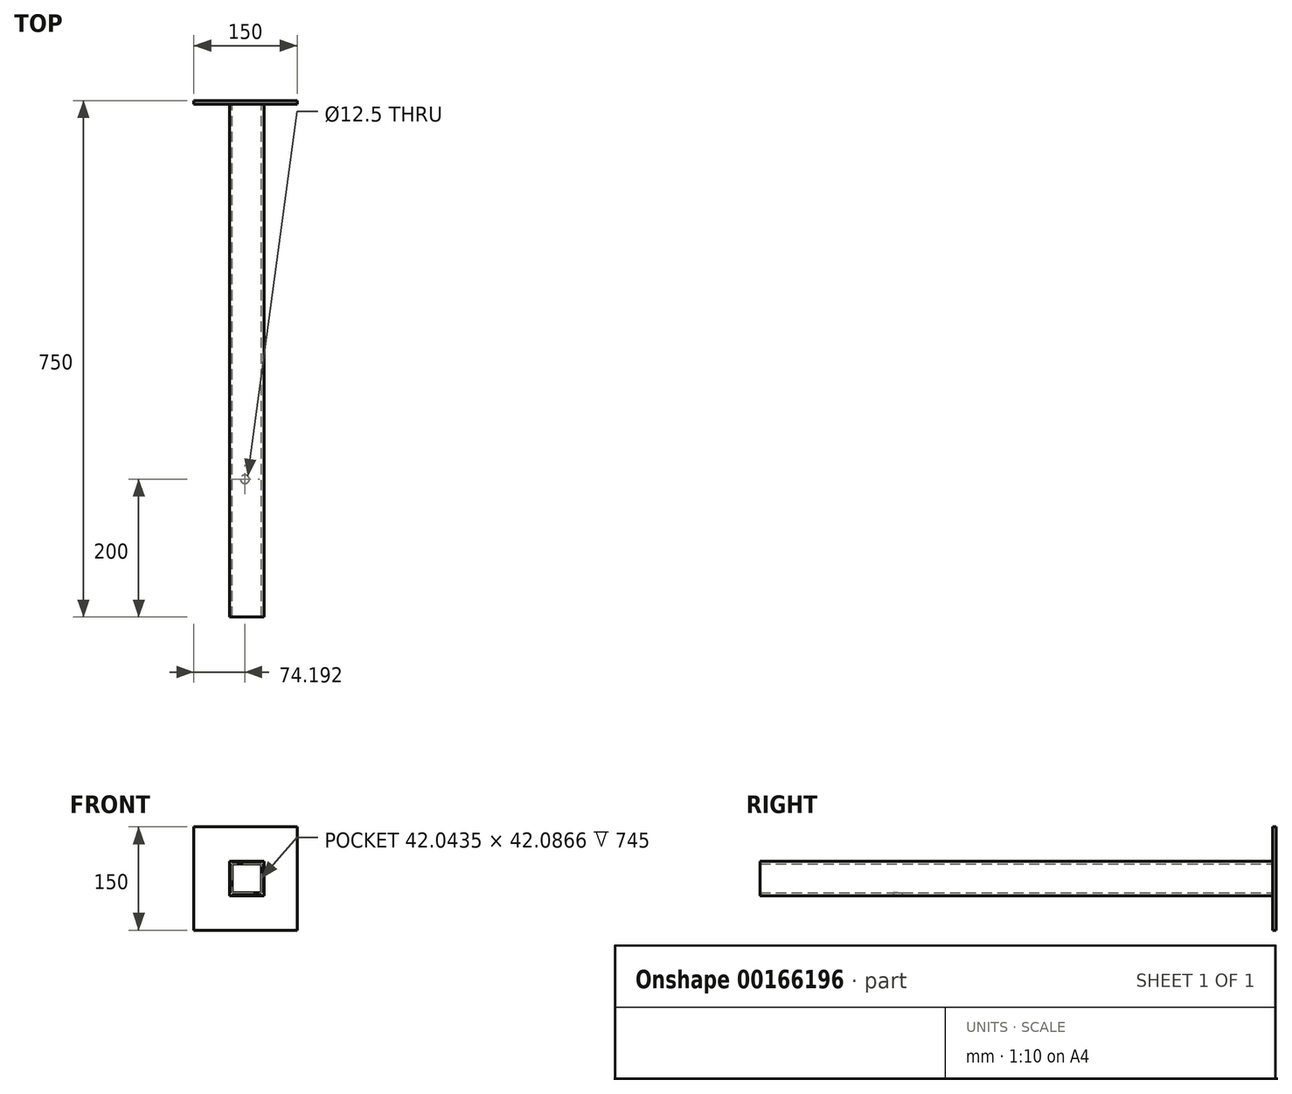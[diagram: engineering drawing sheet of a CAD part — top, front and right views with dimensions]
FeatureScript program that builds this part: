
annotation { "Feature Type Name" : "Feature", "Feature Type Description" : "" }
export const myFeature = defineFeature(function(context is Context, id is Id, definition is map)
    precondition{}
    {
        {
            var Q0;
            Q0=qCreatedBy(makeId("Front.planeOp"),FACE);
            var sketch = newSketch(context, id + "F0", { "sketchPlane" : qUnion([Q0])});
            skLineSegment(sketch, "E0.bottom", {"start": v(-73.02, 50) * mm, "end": v(-23.02, 50) * mm});
            skLineSegment(sketch, "E0.top", {"start": v(-73.02, 0) * mm, "end": v(-23.02, 0) * mm});
            skLineSegment(sketch, "E0.left", {"start": v(-73.02, 50) * mm, "end": v(-73.02, 0) * mm});
            skLineSegment(sketch, "E0.right", {"start": v(-23.02, 50) * mm, "end": v(-23.02, 0) * mm});
            skPoint(sketch, "E1.centerSnap0", {"position": v(-48.02, 50) * mm});
            skLineSegment(sketch, "E2.bottom", {"start": v(-69.17, 46.31) * mm, "end": v(-27.13, 46.31) * mm});
            skLineSegment(sketch, "E2.top", {"start": v(-69.17, 4.23) * mm, "end": v(-27.13, 4.23) * mm});
            skLineSegment(sketch, "E2.left", {"start": v(-69.17, 46.31) * mm, "end": v(-69.17, 4.23) * mm});
            skLineSegment(sketch, "E2.right", {"start": v(-27.13, 46.31) * mm, "end": v(-27.13, 4.23) * mm});
            skSolve(sketch);
        }
        {
            var Q0;
            Q0 = qSketchRegion(id + "F0", true);
            extrude(context, id + "F1", {"entities" : qUnion([Q0]), "depth" : 750 * mm});
        }
        {
            var Q0;
            Q0=qCreatedBy(makeId("Front.planeOp"),FACE);
            var sketch = newSketch(context, id + "F2", { "sketchPlane" : qUnion([Q0])});
            skLineSegment(sketch, "E3.bottom", {"start": v(24.88, -50.14) * mm, "end": v(-125.12, -50.14) * mm});
            skLineSegment(sketch, "E3.top", {"start": v(24.88, 99.86) * mm, "end": v(-125.12, 99.86) * mm});
            skLineSegment(sketch, "E3.left", {"start": v(24.88, -50.14) * mm, "end": v(24.88, 99.86) * mm});
            skLineSegment(sketch, "E3.right", {"start": v(-125.12, -50.14) * mm, "end": v(-125.12, 99.86) * mm});
            skSolve(sketch);
        }
        {
            var Q0;
            Q0=makeQuery(id+"F2.imprint","IMPRINT",FACE,{"disambiguationData":[TD([[makeQuery(id+"F2.imprint","IMPRINT",EDGE,{"derivedFrom":sQuery(id+"F2.wireOp",EDGE,"E3.bottom")}),-1.0]])]});
            extrude(context, id + "F3", {"entities" : qUnion([Q0]), "operationType" : NewBodyOperationType.ADD, "depth" : 5 * mm});
        }
        {
            var Q0;
            Q0=makeQuery(id+"F1.opExtrude","SWEPT_FACE",FACE,{"disambiguationData":[OSD([sQuery(id+"F0.wireOp",EDGE,"E0.top")])]});
            var sketch = newSketch(context, id + "F4", { "sketchPlane" : qUnion([Q0])});
            skCircle(sketch, "E4", {"center": v(-50.93, 550) * mm, "radius": 6.25 * mm});
            skSolve(sketch);
        }
        {
            var Q0;
            Q0=makeQuery(id+"F4.imprint","IMPRINT",FACE,{"disambiguationData":[TD([[makeQuery(id+"F4.imprint","IMPRINT",EDGE,{"derivedFrom":sQuery(id+"F4.wireOp",EDGE,"E4")}),1.0]])]});
            extrude(context, id + "F5", {"entities" : qUnion([Q0]), "operationType" : NewBodyOperationType.REMOVE, "oppositeDirection" : true, "depth" : 25 * mm});
        }
    });
